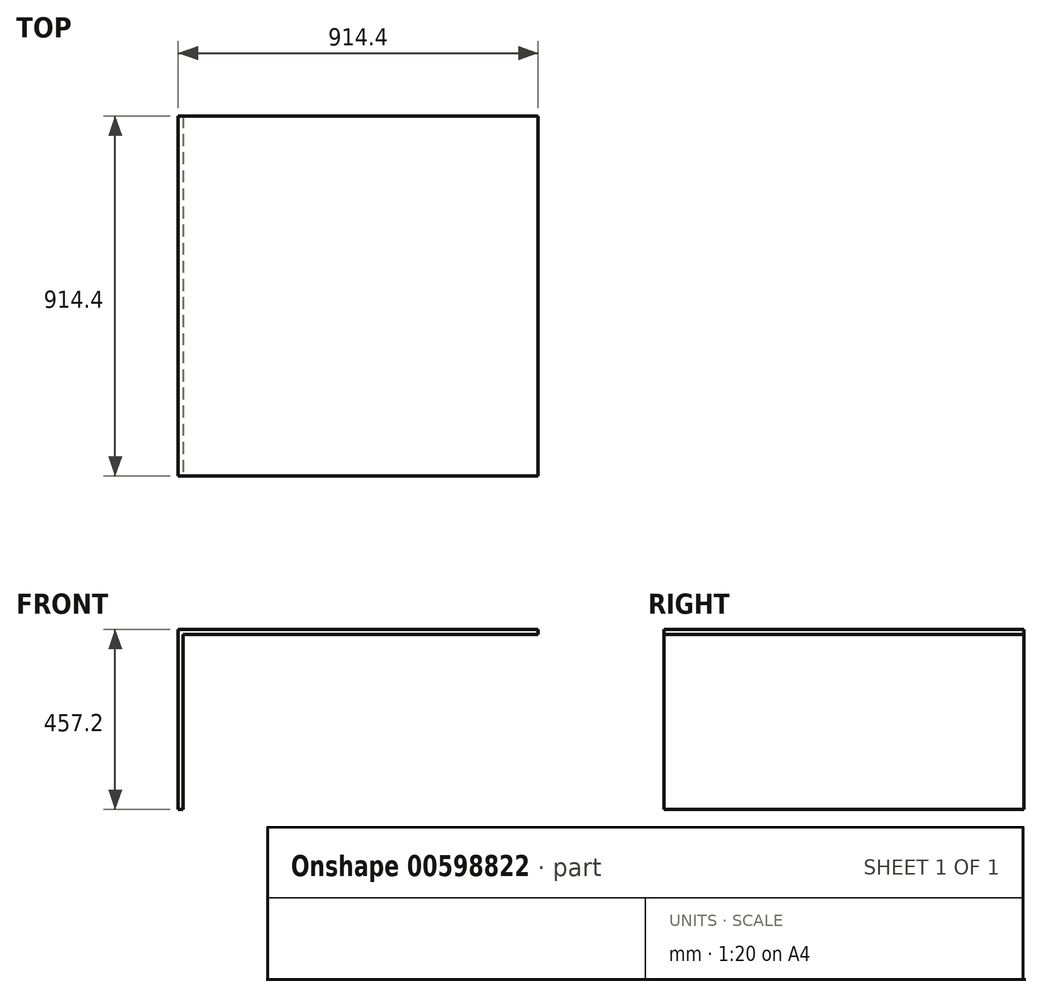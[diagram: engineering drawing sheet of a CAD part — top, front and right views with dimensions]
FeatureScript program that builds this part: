
annotation { "Feature Type Name" : "Feature", "Feature Type Description" : "" }
export const myFeature = defineFeature(function(context is Context, id is Id, definition is map)
    precondition{}
    {
        {
            var Q0;
            Q0=qCreatedBy(makeId("Front.planeOp"),FACE);
            var sketch = newSketch(context, id + "F0", { "sketchPlane" : qUnion([Q0])});
            skLineSegment(sketch, "E0", {"start": v(-455.2, 381.86) * mm, "end": v(459.2, 381.86) * mm});
            skLineSegment(sketch, "E1", {"start": v(459.2, 381.86) * mm, "end": v(459.2, 369.16) * mm});
            skLineSegment(sketch, "E2", {"start": v(-455.2, 381.86) * mm, "end": v(-455.2, -75.34) * mm});
            skLineSegment(sketch, "E3", {"start": v(-455.2, -75.34) * mm, "end": v(-442.5, -75.34) * mm});
            skLineSegment(sketch, "E4", {"start": v(459.2, 369.16) * mm, "end": v(-442.5, 369.16) * mm});
            skLineSegment(sketch, "E5", {"start": v(-442.5, 369.16) * mm, "end": v(-442.5, -75.34) * mm});
            skSolve(sketch);
        }
        {
            var Q0;
            Q0=makeQuery(id+"F0.imprint","IMPRINT",FACE,{"disambiguationData":[TD([[makeQuery(id+"F0.imprint","IMPRINT",EDGE,{"derivedFrom":sQuery(id+"F0.wireOp",EDGE,"E0")}),-1.0]])]});
            extrude(context, id + "F1", {"entities" : qUnion([Q0]), "oppositeDirection" : true, "depth" : 914.4 * mm, "offsetDistance" : 25.4 * mm});
        }
    });
